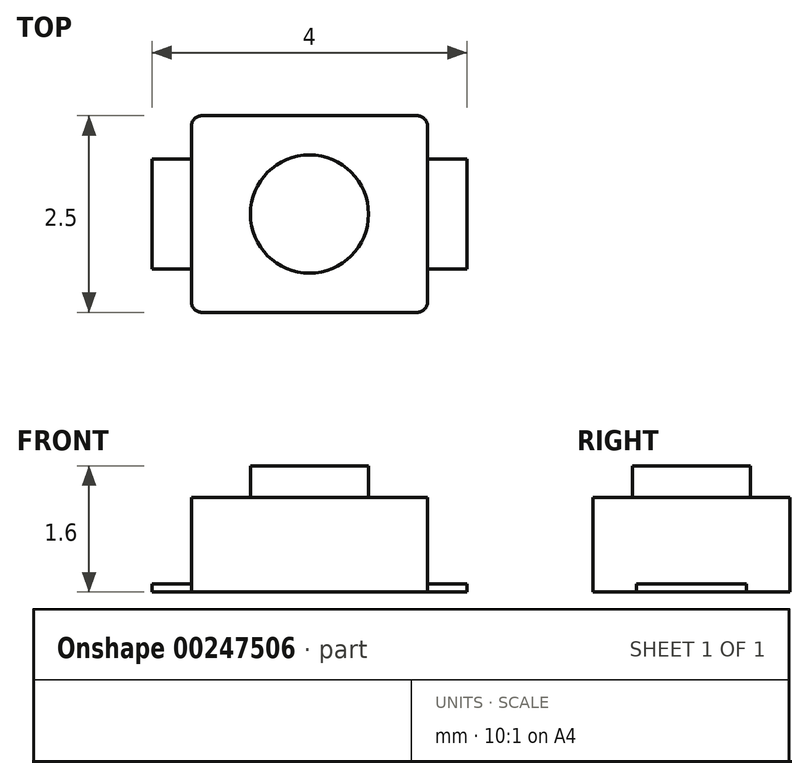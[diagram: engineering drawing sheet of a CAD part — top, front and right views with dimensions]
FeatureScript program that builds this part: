
annotation { "Feature Type Name" : "Feature", "Feature Type Description" : "" }
export const myFeature = defineFeature(function(context is Context, id is Id, definition is map)
    precondition{}
    {
        {
            var Q0;
            Q0=qCreatedBy(makeId("Top.planeOp"),FACE);
            var sketch = newSketch(context, id + "F0", { "sketchPlane" : qUnion([Q0])});
            skLineSegment(sketch, "E0.bottom", {"start": v(1.36, -1.25) * mm, "end": v(-1.36, -1.25) * mm});
            skLineSegment(sketch, "E0.top", {"start": v(1.36, 1.25) * mm, "end": v(-1.36, 1.25) * mm});
            skLineSegment(sketch, "E0.left", {"start": v(1.5, -1.11) * mm, "end": v(1.5, 1.11) * mm});
            skLineSegment(sketch, "E0.right", {"start": v(-1.5, -1.11) * mm, "end": v(-1.5, 1.11) * mm});
            skPoint(sketch, "E0.middle", {"position": v(0, 0) * mm});
            skPoint(sketch, "E1.visualSharp", {"position": v(-1.5, 1.25) * mm});
            skArc(sketch, "E1.filletArc", {"start": v(-1.36, 1.25) * mm, "mid": v(-1.46, 1.21) * mm, "end": v(-1.5, 1.11) * mm});
            skPoint(sketch, "E2.visualSharp", {"position": v(1.5, 1.25) * mm});
            skArc(sketch, "E2.filletArc", {"start": v(1.5, 1.11) * mm, "mid": v(1.46, 1.21) * mm, "end": v(1.36, 1.25) * mm});
            skPoint(sketch, "E3.visualSharp", {"position": v(1.5, -1.25) * mm});
            skArc(sketch, "E3.filletArc", {"start": v(1.36, -1.25) * mm, "mid": v(1.46, -1.21) * mm, "end": v(1.5, -1.11) * mm});
            skPoint(sketch, "E4.visualSharp", {"position": v(-1.5, -1.25) * mm});
            skArc(sketch, "E4.filletArc", {"start": v(-1.5, -1.11) * mm, "mid": v(-1.46, -1.21) * mm, "end": v(-1.36, -1.25) * mm});
            skSolve(sketch);
        }
        {
            var Q0;
            Q0=qSketchRegion(id+"F0",true);
            extrude(context, id + "F1", {"entities" : qUnion([Q0]), "depth" : 1.2 * mm});
        }
        {
            var Q0;
            Q0=makeQuery(id+"F1.opExtrude","CAP_FACE",FACE,{"disambiguationData":[OSD([sQuery(id+"F0.wireOp",EDGE,"E0.bottom"),sQuery(id+"F0.wireOp",EDGE,"E0.top"),sQuery(id+"F0.wireOp",EDGE,"E0.left"),sQuery(id+"F0.wireOp",EDGE,"E0.right"),sQuery(id+"F0.wireOp",EDGE,"E1.filletArc"),sQuery(id+"F0.wireOp",EDGE,"E2.filletArc"),sQuery(id+"F0.wireOp",EDGE,"E3.filletArc"),sQuery(id+"F0.wireOp",EDGE,"E4.filletArc")])],"isStart":false});
            var sketch = newSketch(context, id + "F2", { "sketchPlane" : qUnion([Q0])});
            skCircle(sketch, "E5", {"center": v(0, 0) * mm, "radius": 0.75 * mm});
            skSolve(sketch);
        }
        {
            var Q0;
            Q0=qSketchRegion(id+"F2",true);
            extrude(context, id + "F3", {"entities" : qUnion([Q0]), "depth" : 0.4 * mm});
        }
        {
            var Q0;
            Q0=makeQuery(id+"F1.opExtrude","CAP_FACE",FACE,{"disambiguationData":[OSD([sQuery(id+"F0.wireOp",EDGE,"E0.bottom"),sQuery(id+"F0.wireOp",EDGE,"E0.top"),sQuery(id+"F0.wireOp",EDGE,"E0.left"),sQuery(id+"F0.wireOp",EDGE,"E0.right"),sQuery(id+"F0.wireOp",EDGE,"E1.filletArc"),sQuery(id+"F0.wireOp",EDGE,"E2.filletArc"),sQuery(id+"F0.wireOp",EDGE,"E3.filletArc"),sQuery(id+"F0.wireOp",EDGE,"E4.filletArc")])],"isStart":true});
            var sketch = newSketch(context, id + "F4", { "sketchPlane" : qUnion([Q0])});
            skLineSegment(sketch, "E6.bottom", {"start": v(2, -0.7) * mm, "end": v(-2, -0.7) * mm});
            skLineSegment(sketch, "E6.top", {"start": v(2, 0.7) * mm, "end": v(-2, 0.7) * mm});
            skLineSegment(sketch, "E6.left", {"start": v(2, -0.7) * mm, "end": v(2, 0.7) * mm});
            skLineSegment(sketch, "E6.right", {"start": v(-2, -0.7) * mm, "end": v(-2, 0.7) * mm});
            skPoint(sketch, "E6.middle", {"position": v(0, 0) * mm});
            skSolve(sketch);
        }
        {
            var Q0;
            Q0=qSketchRegion(id+"F4",true);
            extrude(context, id + "F5", {"entities" : qUnion([Q0]), "operationType" : NewBodyOperationType.ADD, "oppositeDirection" : true, "depth" : .1 * mm});
        }
    });
